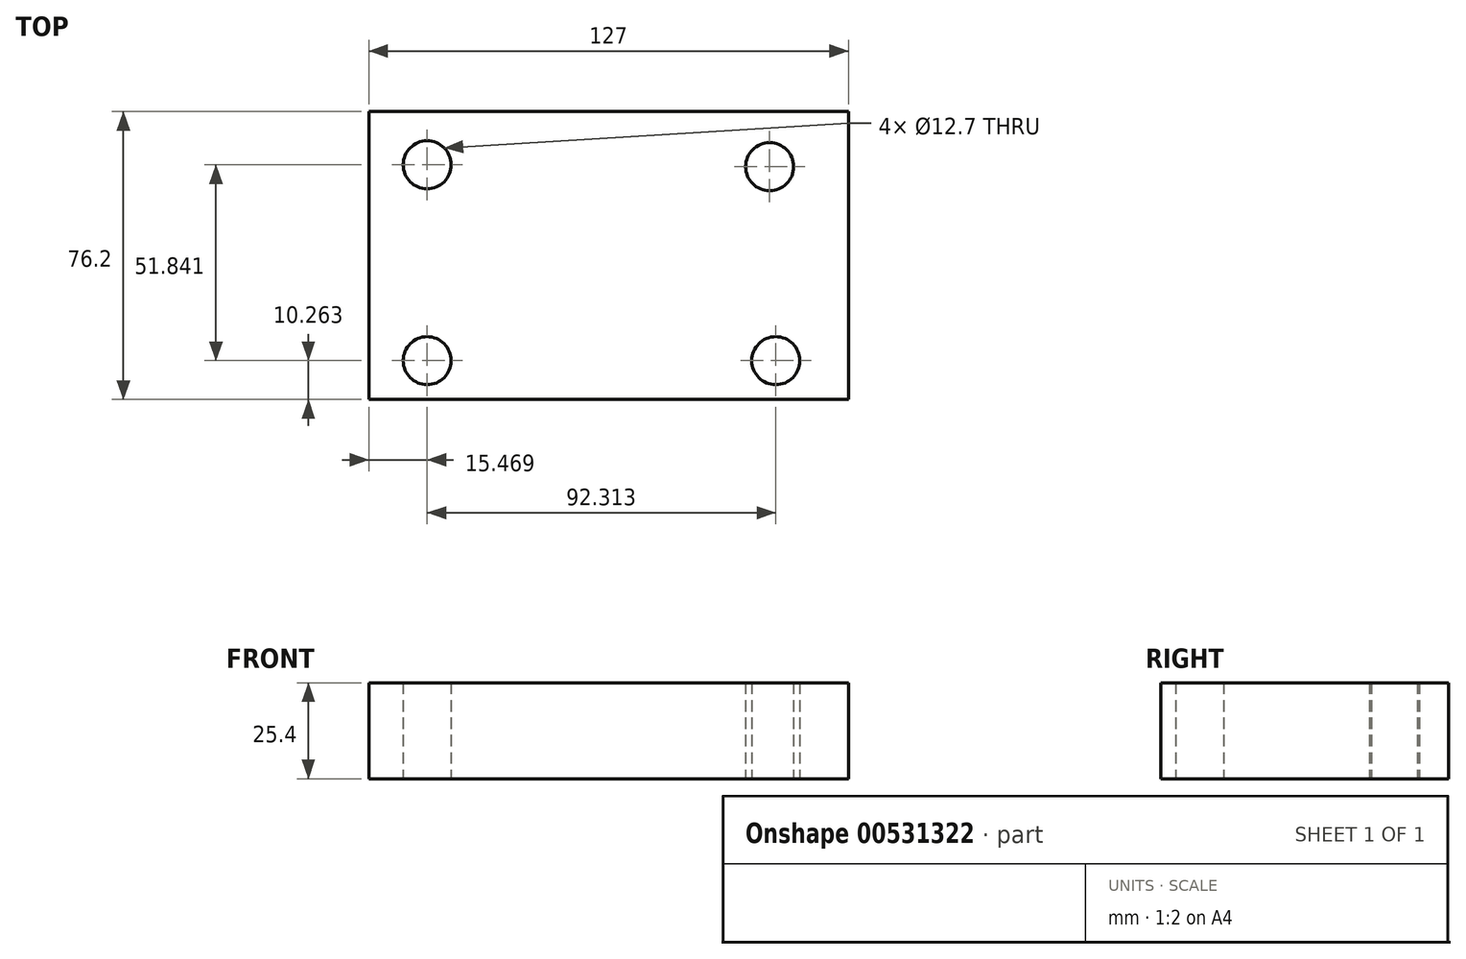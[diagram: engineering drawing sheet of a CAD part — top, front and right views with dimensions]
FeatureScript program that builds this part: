
annotation { "Feature Type Name" : "Feature", "Feature Type Description" : "" }
export const myFeature = defineFeature(function(context is Context, id is Id, definition is map)
    precondition{}
    {
        {
            var Q0;
            Q0=qCreatedBy(makeId("Top.planeOp"),FACE);
            var sketch = newSketch(context, id + "F0", { "sketchPlane" : qUnion([Q0])});
            skLineSegment(sketch, "E0.bottom", {"start": v(-63.5, -38.1) * mm, "end": v(63.5, -38.1) * mm});
            skLineSegment(sketch, "E0.top", {"start": v(-63.5, 38.1) * mm, "end": v(63.5, 38.1) * mm});
            skLineSegment(sketch, "E0.left", {"start": v(-63.5, -38.1) * mm, "end": v(-63.5, 38.1) * mm});
            skLineSegment(sketch, "E0.right", {"start": v(63.5, -38.1) * mm, "end": v(63.5, 38.1) * mm});
            skPoint(sketch, "E0.middle", {"position": v(0, 0) * mm});
            skSolve(sketch);
        }
        {
            var Q0;
            Q0=makeQuery(id+"F0.imprint","IMPRINT",FACE,{"disambiguationData":[TD([[makeQuery(id+"F0.imprint","IMPRINT",EDGE,{"derivedFrom":sQuery(id+"F0.wireOp",EDGE,"E0.bottom")}),1.0]])]});
            extrude(context, id + "F1", {"entities" : qUnion([Q0]), "depth" : 25.4 * mm, "offsetDistance" : 25.4 * mm});
        }
        {
            var Q0;
            Q0=qCreatedBy(makeId("Top.planeOp"),FACE);
            var sketch = newSketch(context, id + "F2", { "sketchPlane" : qUnion([Q0])});
            skCircle(sketch, "E1", {"center": v(-48.03, -27.84) * mm, "radius": 6.35 * mm});
            skCircle(sketch, "E2", {"center": v(44.28, -27.84) * mm, "radius": 6.35 * mm});
            skCircle(sketch, "E3", {"center": v(42.66, 23.52) * mm, "radius": 6.35 * mm});
            skCircle(sketch, "E4", {"center": v(-48.03, 24) * mm, "radius": 6.35 * mm});
            skSolve(sketch);
        }
        {
            var Q0;
            Q0 = qSketchRegion(id + "F2", true);
            extrude(context, id + "F3", {"entities" : qUnion([Q0]), "operationType" : NewBodyOperationType.REMOVE, "endBound" : BoundingType.THROUGH_ALL, "depth" : 25.4 * mm, "offsetDistance" : 25.4 * mm});
        }
    });
